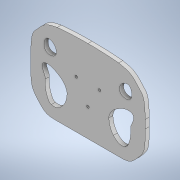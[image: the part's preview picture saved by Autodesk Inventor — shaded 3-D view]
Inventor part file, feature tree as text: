
AUTODESK INVENTOR PART (.ipt)
format: ipt  version: 2021 (Build 250183000, 183)  size: 199,680 bytes
history: native  units: in
note: dims shown in document units (in); Inventor stores cm internally (conversion verified against a paired STEP export)
features: extrude x3, sketch x3
ambient origin geometry x8: Origin, YZ Plane, XZ Plane, XY Plane, X Axis, Y Axis, Z Axis, Center Point
bodies: Solid1 (feature_tree)
feature tree (6):
  extrude  "Extrusion1"  Depth=1.998in
  extrude  "Extrusion2"  Depth=1.1811in TaperAngle=360.0deg
  extrude  "Extrusion3"  Depth=0.3in TaperAngle=0.0deg
  sketch  "Sketch1"  dims[d1=0.3in d2=0.0in d4=1.998in]
  sketch  "Sketch2"  dims[d5=0.185in d6=1.1811in d8=360.0deg]
  sketch  "Sketch3"  dims[d10=3.125in d11=0.0in d12=0.3in d13=0.0in]
